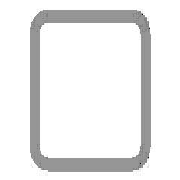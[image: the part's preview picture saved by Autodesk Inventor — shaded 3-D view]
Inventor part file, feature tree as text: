
AUTODESK INVENTOR PART (.ipt)
format: ipt  version: 2024 (Build 280153000, 153)  size: 150,528 bytes
history: native  units: mm (DEFAULTED — no unit token found)
features: other x4, plane x3, split x2, extrude x1, sketch x1
ambient origin geometry x8: Origin, YZ Plane, XZ Plane, XY Plane, X Axis, Y Axis, Z Axis, Center Point
bodies: Solid1 (feature_tree)
feature tree (11):
  parser-record x1  (decoder bookkeeping rows leaked as tree rows — omitted from the tree; the rows remain in map.json)
  other  "Driven Length"
  other  "Plano inicial"
  other  "Plano final"
  extrude  "Cuerpo"  TaperAngle=0.0deg  [1 undecoded]
  plane  "Plano de trabajo4"
  split  "Dividir1"
  plane  "Plano de trabajo5"
  split  "Dividir2"
  sketch  "Sketch3"  dims[d3=2240.8mm d4=0.0mm d10=50.8mm d11=50.8mm d12=3.175mm d13=-25.4mm d14=2215.4mm d15=25.4mm d16=25.4mm d17=6.35mm d18=90.0deg d19=2240.8mm]
  plane  "Work Plane3"
note: 1 required parameter value undecoded (feature->parameter linkage not recoverable at this tier; creation-order binding heuristic only, values carry confidence <= 0.55)
